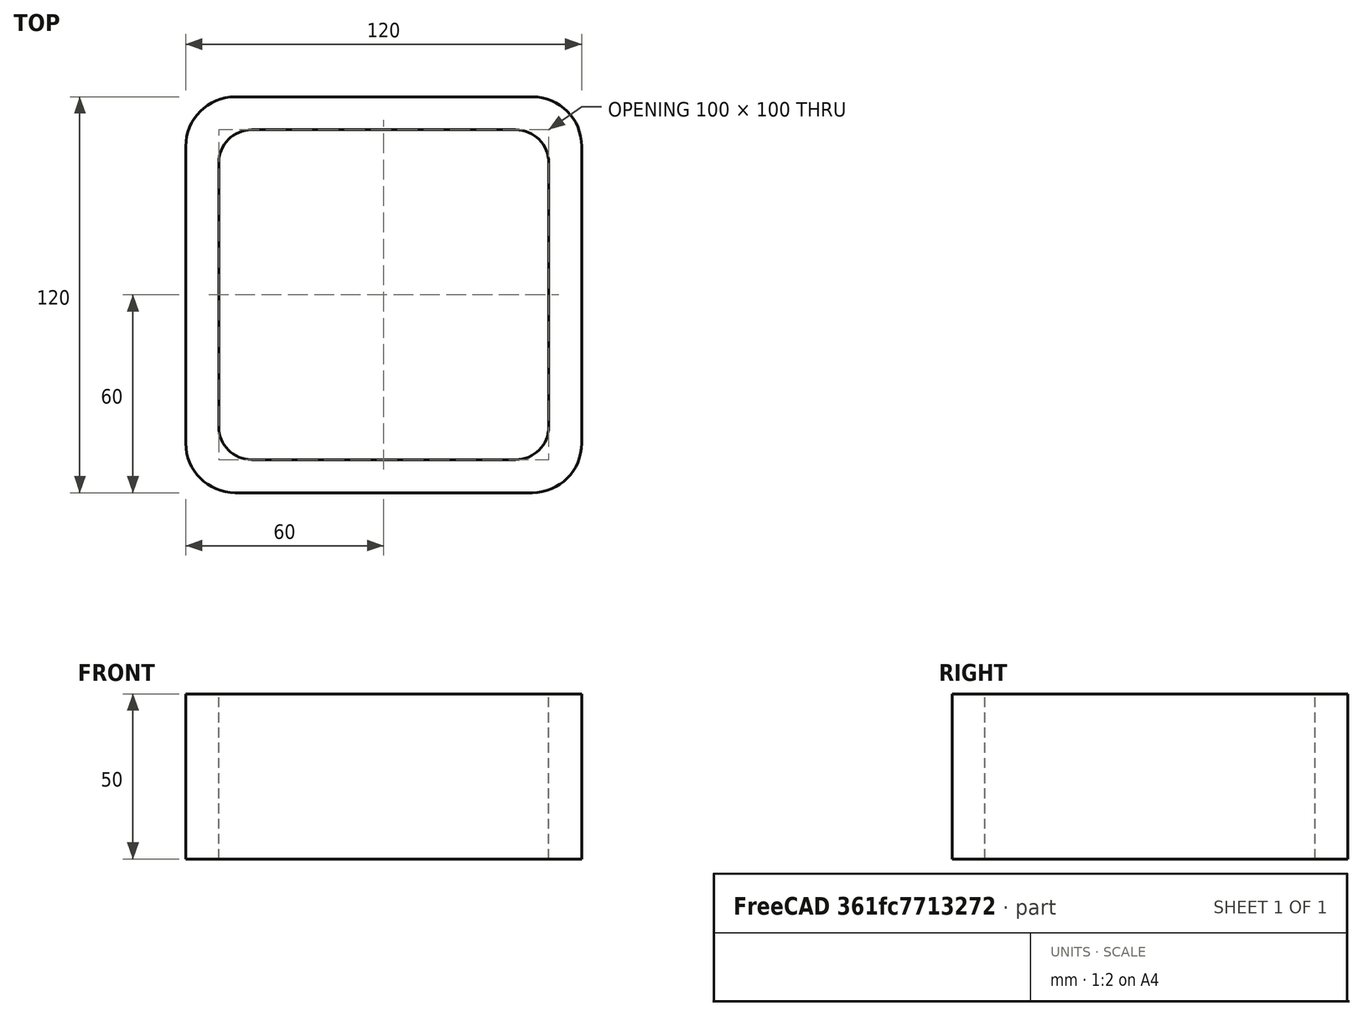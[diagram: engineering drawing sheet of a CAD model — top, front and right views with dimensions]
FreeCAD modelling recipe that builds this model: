
FCSTD DOCUMENT  (FreeCAD 0.15R4671 (Git))
Label: Square hollow section 120x120x10 EN10219 S235JRH
License: All rights reserved
LicenseURL: http://en.wikipedia.org/wiki/All_rights_reserved
objects: Sketcher::SketchObject×1, Part::Extrusion×1
note: 2 computed .brp shape members not serialized (recipe doc carries the construction recipe); baked Part::Feature solids carry a one-line shape summary decoded from their .brp

FEATURE [Sketcher::SketchObject] Sketch
  sketch-geometry (16):
    g0: LineSegment StartX=-40 StartY=50 StartZ=0 EndX=40 EndY=50 EndZ=0
    g1: LineSegment StartX=50 StartY=40 StartZ=0 EndX=50 EndY=-40 EndZ=0
    g2: LineSegment StartX=40 StartY=-50 StartZ=0 EndX=-40 EndY=-50 EndZ=0
    g3: LineSegment StartX=-50 StartY=-40 StartZ=0 EndX=-50 EndY=40 EndZ=0
    g4: LineSegment StartX=-45 StartY=60 StartZ=0 EndX=45 EndY=60 EndZ=0
    g5: LineSegment StartX=60 StartY=45 StartZ=0 EndX=60 EndY=-45 EndZ=0
    g6: LineSegment StartX=45 StartY=-60 StartZ=0 EndX=-45 EndY=-60 EndZ=0
    g7: LineSegment StartX=-60 StartY=-45 StartZ=0 EndX=-60 EndY=45 EndZ=0
    g8: ArcOfCircle CenterX=-40 CenterY=40 CenterZ=0 NormalX=0 NormalY=0 NormalZ=1 Radius=10 StartAngle=1.5708 EndAngle=3.14159
    g9: ArcOfCircle CenterX=40 CenterY=40 CenterZ=0 NormalX=0 NormalY=0 NormalZ=1 Radius=10 StartAngle=0 EndAngle=1.5708
    g10: ArcOfCircle CenterX=40 CenterY=-40 CenterZ=0 NormalX=0 NormalY=0 NormalZ=1 Radius=10 StartAngle=4.71239 EndAngle=6.28319
    g11: ArcOfCircle CenterX=-40 CenterY=-40 CenterZ=0 NormalX=0 NormalY=0 NormalZ=1 Radius=10 StartAngle=3.14159 EndAngle=4.71239
    g12: ArcOfCircle CenterX=45 CenterY=45 CenterZ=0 NormalX=0 NormalY=0 NormalZ=1 Radius=15 StartAngle=0 EndAngle=1.5708
    g13: ArcOfCircle CenterX=45 CenterY=-45 CenterZ=0 NormalX=0 NormalY=0 NormalZ=1 Radius=15 StartAngle=4.71239 EndAngle=6.28319
    g14: ArcOfCircle CenterX=-45 CenterY=-45 CenterZ=0 NormalX=0 NormalY=0 NormalZ=1 Radius=15 StartAngle=3.14159 EndAngle=4.71239
    g15: ArcOfCircle CenterX=-45 CenterY=45 CenterZ=0 NormalX=0 NormalY=0 NormalZ=1 Radius=15 StartAngle=1.5708 EndAngle=3.14159
  constraints (36):
    c: Horizontal(g2)
    c: Vertical(g3)
    c: Horizontal(g6)
    c: Vertical(g7)
    c: Tangent(g3,g8) = 1.5708
    c: Tangent(g0,g8) = 1.5708
    c: Tangent(g0,g9) = 1.5708
    c: Tangent(g1,g9) = 1.5708
    c: Tangent(g1,g10) = 1.5708
    c: Tangent(g2,g10) = 1.5708
    c: Tangent(g2,g11) = 1.5708
    c: Tangent(g3,g11) = 1.5708
    c: Tangent(g4,g12) = 1.5708
    c: Tangent(g5,g12) = 1.5708
    c: Tangent(g5,g13) = 1.5708
    c: Tangent(g6,g13) = 1.5708
    c: Tangent(g6,g14) = 1.5708
    c: Tangent(g7,g14) = 1.5708
    c: Tangent(g7,g15) = 1.5708
    c: Tangent(g4,g15) = 1.5708
    c: Equal(g9,g8)
    c: Equal(g9,g11)
    c: Equal(g9,g10)
    c: Equal(g12,g15)
    c: Equal(g12,g14)
    c: Equal(g12,g13)
    c: Symmetric(g4,g6,g-1)
    c: Symmetric(g7,g5,g-2)
    c: DistanceY(g4,g6) = -120
    c: DistanceX(g7,g5) = 120
    c: Symmetric(g3,g1,g-2)
    c: Symmetric(g0,g2,g-1)
    c: DistanceY(g0,g4) = 10
    c: DistanceX(g5,g1) = -10
    c: Radius(g9) = 10
    c: Radius(g12) = 15
FEATURE [Part::Extrusion] Extrude  label="Square hollow section 120x120x10 EN10219 S235JRH"
  Base = -> Sketch
  Dir = (0,0,50)
  Solid = true
